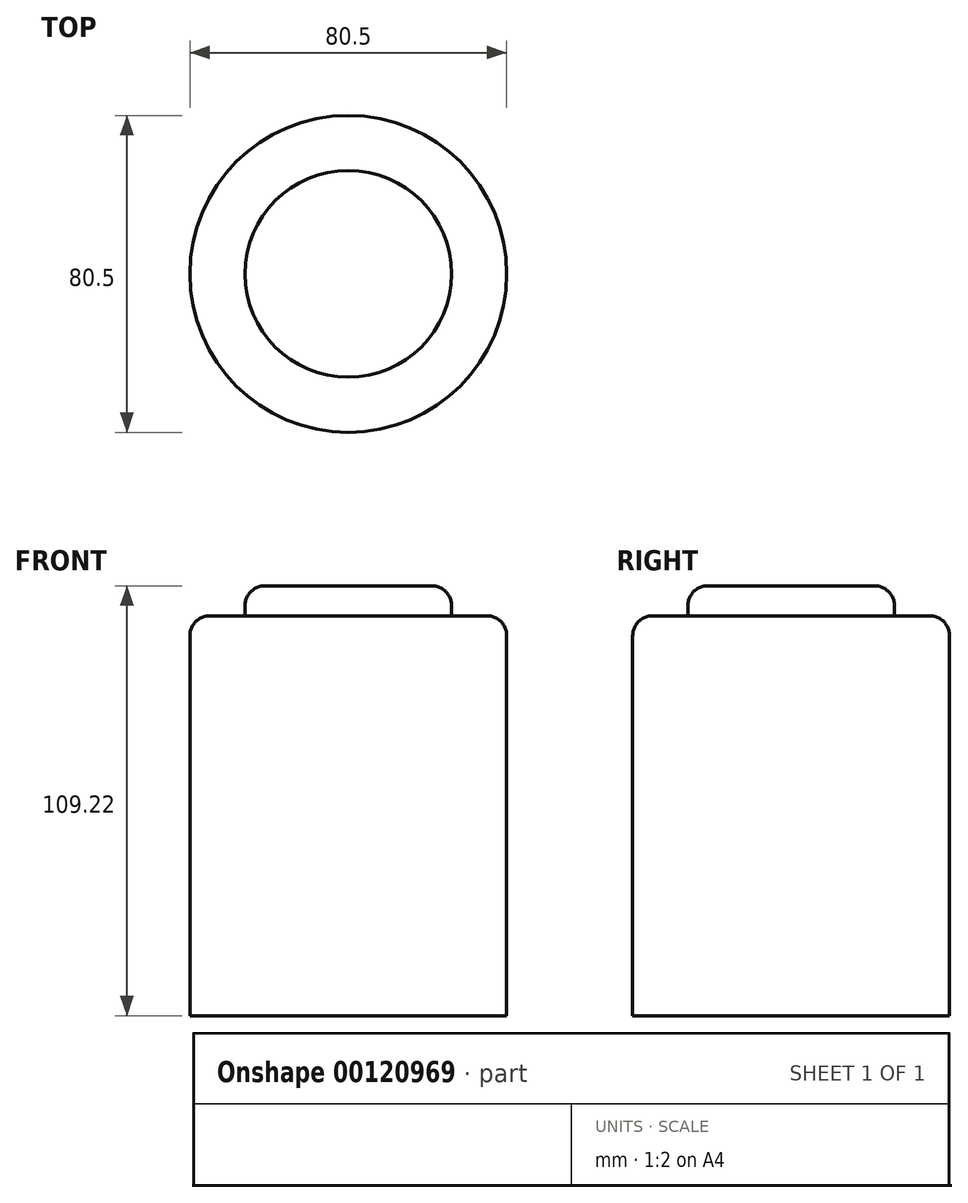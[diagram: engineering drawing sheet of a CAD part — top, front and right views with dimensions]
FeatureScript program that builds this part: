
annotation { "Feature Type Name" : "Feature", "Feature Type Description" : "" }
export const myFeature = defineFeature(function(context is Context, id is Id, definition is map)
    precondition{}
    {
        {
            var Q0;
            Q0=qCreatedBy(makeId("Top.planeOp"),FACE);
            var sketch = newSketch(context, id + "F0", { "sketchPlane" : qUnion([Q0])});
            skCircle(sketch, "E0", {"center": v(0, 0) * mm, "radius": 40.25 * mm});
            skSolve(sketch);
        }
        {
            var Q0;
            Q0 = qSketchRegion(id + "F0", true);
            extrude(context, id + "F1", {"entities" : qUnion([Q0]), "depth" : 101.6 * mm});
        }
        {
            var Q0;
            Q0=makeQuery(id+"F1.opExtrude","CAP_FACE",FACE,{"disambiguationData":[OSD([sQuery(id+"F0.wireOp",EDGE,"E0")])],"isStart":false});
            var sketch = newSketch(context, id + "F2", { "sketchPlane" : qUnion([Q0])});
            skCircle(sketch, "E1", {"center": v(0, 0) * mm, "radius": 26.25 * mm});
            skSolve(sketch);
        }
        {
            var Q0;
            Q0 = qSketchRegion(id + "F2", true);
            extrude(context, id + "F3", {"entities" : qUnion([Q0]), "operationType" : NewBodyOperationType.ADD, "depth" : 7.62 * mm});
        }
        {
            var Q0;
            Q0=makeQuery(id+"F3.opExtrude","CAP_FACE",FACE,{"disambiguationData":[OSD([sQuery(id+"F2.wireOp",EDGE,"E1")])],"isStart":false});
            fillet(context, id + "F4", {"entities" : qUnion([Q0]), "radius" : 5.08 * mm, "tangentPropagation" : true, "allowEdgeOverflow" : false});
        }
        {
            var Q0;
            Q0=makeQuery(id+"F1.opExtrude","CAP_EDGE",EDGE,{"disambiguationData":[OSD([sQuery(id+"F0.wireOp",EDGE,"E0")])],"isStart":false});
            fillet(context, id + "F5", {"entities" : qUnion([Q0]), "radius" : 5.08 * mm, "tangentPropagation" : true, "allowEdgeOverflow" : false});
        }
    });
